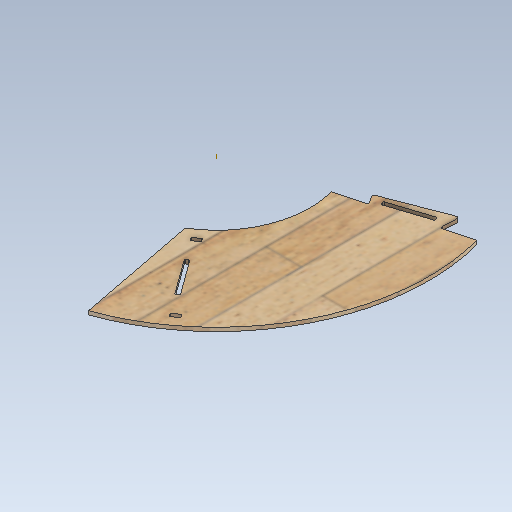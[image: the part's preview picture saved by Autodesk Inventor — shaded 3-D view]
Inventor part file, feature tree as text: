
AUTODESK INVENTOR PART (.ipt)
format: ipt  version: 2020 (Build 240168000, 168)  size: 451,072 bytes
history: native  units: mm
features: extrude x5, sketch x4, pattern_circular x3, mirror x1
ambient origin geometry x8: Origin, YZ Plane, XZ Plane, XY Plane, X Axis, Y Axis, Z Axis, Center Point
bodies: Body1 (feature_tree)
feature tree (13):
  extrude  "Extrusion3"  Depth=6.5mm
  extrude  "Extrusion4"  Depth=2.666667mm
  extrude  "Extrusion5"  Depth=1.333333mm
  sketch  "Sketch5"  dims[d32=1.333333mm d33=1.333333mm]
  extrude  "Extrusion7"  Depth=145.0mm
  pattern_circular  "Circular Pattern2"  Angle=90.0deg  [1 undecoded]
  pattern_circular  "Circular Pattern3"  [2 undecoded]
  mirror  "Mirror3"
  pattern_circular  "Circular Pattern4"  Angle=90.0deg  [1 undecoded]
  extrude  "Extrusion10"  Depth=145.0mm
  sketch  "Sketch2"  dims[d15=6.0mm d16=0.0mm d21=6.5mm]
  sketch  "Sketch3"  dims[d24=2.666667mm d25=2.666667mm]
  sketch  "Sketch6"  dims[d38=0.0mm d39=0.0mm d40=3.25mm d41=90.0deg d42=3.25mm d43=90.0deg d52=4.363323mm d54=10.0mm d55=0.0mm d60=0.872665mm d61=12.566371mm d62=13.439035mm d63=2.666667mm d64=0.523599mm d66=0.523599mm d67=2.666667mm d68=2.666667mm d70=12.566371mm d71=12.566371mm d84=300.14mm d85=682.72mm d86=491.43mm d87=150.07mm d88=341.36mm d89=4.363323mm d90=1.919862mm d91=1.919862mm d94=300.14mm d95=682.72mm d104=6.5mm d105=12.0mm d108=1.333333mm d109=1.333333mm d110=1.333333mm d111=1.333333mm d112=0.0mm d113=0.0mm d114=0.0mm d145=20.0mm d146=12.566371mm d149=145.0mm d150=90.0deg d151=90.0deg d152=90.0deg d153=90.0deg d154=20.0mm d155=25.132741mm d157=20.0mm d158=25.132741mm d169=0.0mm d170=0.0mm]
note: 4 required parameter values undecoded (feature->parameter linkage not recoverable at this tier; creation-order binding heuristic only, values carry confidence <= 0.55)
